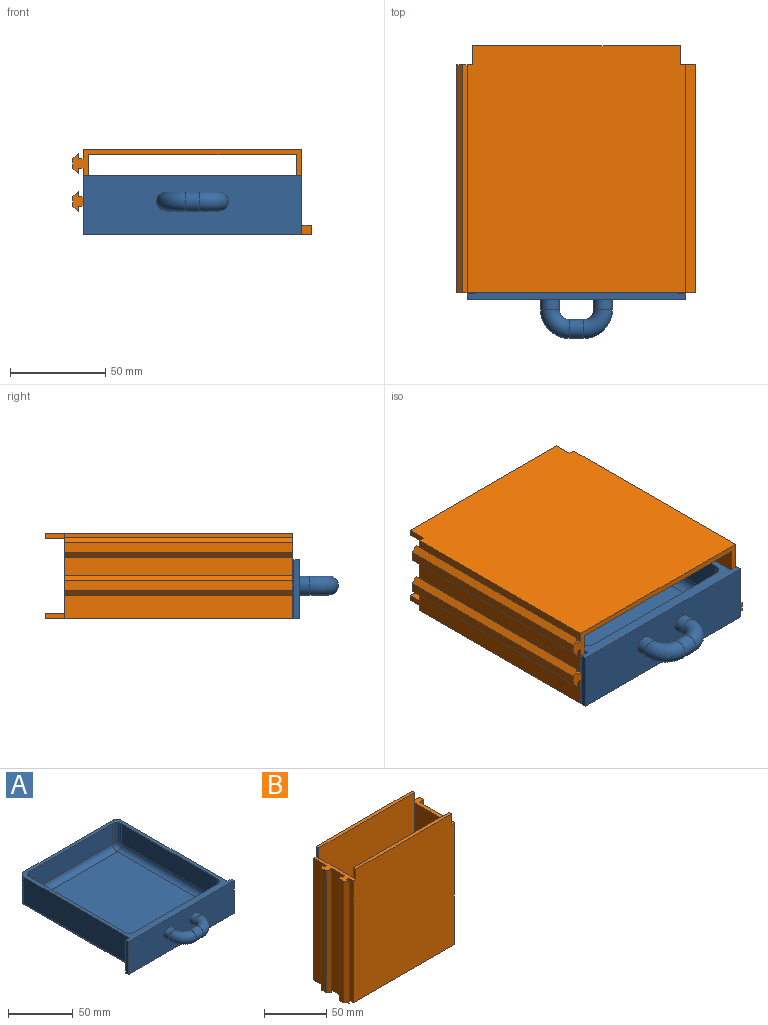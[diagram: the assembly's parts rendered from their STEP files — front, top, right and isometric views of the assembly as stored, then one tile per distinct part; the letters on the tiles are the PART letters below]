
ASSEMBLY  parts=2 mates=2
PART A: 39 faces, bbox 115x145x31 mm
  f0: plane 123x115mm, normal (0,0,1), area 1678.7mm2, adj f2,f3,f4,f6,f7,f8,f9,f10
  f1: plane 118x102.5mm, normal (0,0,-1), area 12091.1mm2, adj f10,f34,f35,f36,f37,f38
  f2: plane 115x25mm, normal (1,0,0), area 2875mm2, adj f0,f10,f27,f38
  f3: plane 115x25mm, normal (-1,0,0), area 2875mm2, adj f0,f10,f28,f34
  f4: plane 96.5x25mm, normal (0,1,0), area 2412.5mm2, adj f0,f27,f28,f36
  f5: plane 104x90.5mm, normal (0,0,1), area 9412mm2, adj f17,f20,f23,f26
  f6: plane 104x19mm, normal (-1,0,0), area 1976mm2, adj f0,f15,f20,f21
  f7: plane 104x19mm, normal (1,0,0), area 1976mm2, adj f0,f16,f22,f23
  f8: plane 90.5x19mm, normal (0,1,0), area 1719.5mm2, adj f0,f21,f22,f26
  f9: plane 90.5x19mm, normal (0,-1,0), area 1719.5mm2, adj f0,f15,f16,f17
  f10: plane 115x31mm, normal (0,1,0), area 691.2mm2, adj f0,f1,f2,f3,f11,f12,f13,f34
  f11: plane 31x3mm, normal (-1,0,0), area 93mm2, adj f0,f10,f12,f14
  f12: plane 115x3mm, normal (0,0,-1), area 345mm2, adj f10,f11,f13,f14
  f13: plane 31x3mm, normal (1,0,0), area 93mm2, adj f0,f10,f12,f14
  f14: plane 115x31mm, normal (0,-1,0), area 3407.9mm2, adj f0,f11,f12,f13,f29,f33
  f15: cylinder r=5mm len=19mm, axis (0,0,-1), area 149.2mm2, adj f0,f6,f9,f18
  f16: cylinder r=5mm len=19mm, axis (0,0,1), area 149.2mm2, adj f0,f7,f9,f19
  f17: cylinder r=5mm len=90.5mm, axis (-1,0,0), area 710.8mm2, adj f5,f9,f18,f19
  f18: sphere r=5mm, area 39.3mm2, adj f15,f17,f20
  f19: sphere r=5mm, area 39.3mm2, adj f16,f17,f23
  f20: cylinder r=5mm len=104mm, axis (0,1,0), area 816.8mm2, adj f5,f6,f18,f24
  f21: cylinder r=5mm len=19mm, axis (0,0,1), area 149.2mm2, adj f0,f6,f8,f24
  f22: cylinder r=5mm len=19mm, axis (0,0,-1), area 149.2mm2, adj f0,f7,f8,f25
  f23: cylinder r=5mm len=104mm, axis (0,-1,0), area 816.8mm2, adj f5,f7,f19,f25
  f24: sphere r=5mm, area 39.3mm2, adj f20,f21,f26
  f25: sphere r=5mm, area 39.3mm2, adj f22,f23,f26
  f26: cylinder r=5mm len=90.5mm, axis (1,0,0), area 710.8mm2, adj f5,f8,f24,f25
  f27: cylinder r=5mm len=25mm, axis (0,0,1), area 196.3mm2, adj f0,f2,f4,f37
  f28: cylinder r=5mm len=25mm, axis (0,0,-1), area 196.3mm2, adj f0,f3,f4,f35
  f29: cylinder r=5mm len=10mm, axis (0,-1,0), area 169.4mm2, adj f14,f30
  f30: torus R=10mm, axis (0,0,1), area 493.5mm2, adj f29,f31
  f31: cylinder r=5mm len=10mm, axis (1,0,0), area 245.2mm2, adj f30,f32
  f32: torus R=10mm, axis (0,0,1), area 493.5mm2, adj f31,f33
  f33: cylinder r=5mm len=10mm, axis (0,1,0), area 169.4mm2, adj f14,f32
  f34: cylinder r=2mm len=115mm, axis (0,1,0), area 361.3mm2, adj f1,f3,f10,f35
  f35: torus R=3mm, axis (0,0,-1), area 21.1mm2, adj f1,f28,f34,f36
  f36: cylinder r=2mm len=96.5mm, axis (1,0,0), area 303.2mm2, adj f1,f4,f35,f37
  f37: torus R=3mm, axis (0,0,-1), area 21.1mm2, adj f1,f27,f36,f38
  f38: cylinder r=2mm len=115mm, axis (0,-1,0), area 361.3mm2, adj f1,f2,f10,f37
PART B: 35 faces, bbox 125.5x45x130 mm
  f0: plane 130x120mm, normal (0,1,0), area 15490mm2, adj f14,f20,f24,f28,f29,f31,f32,f34
  f1: plane 120x3mm, normal (-0.71,-0.71,0), area 509.1mm2, adj f2,f18,f28,f31
  f2: plane 120x5mm, normal (-1,0,0), area 600mm2, adj f1,f3,f28,f31
  f3: plane 120x3mm, normal (-0.71,0.71,0), area 509.1mm2, adj f2,f4,f28,f31
  f4: plane 120x3mm, normal (1,0,0), area 360mm2, adj f3,f5,f28,f31
  f5: plane 120x2.5mm, normal (0,1,0), area 300mm2, adj f4,f6,f28,f31
  f6: plane 120x15mm, normal (-1,0,0), area 1800mm2, adj f5,f7,f28,f31
  f7: plane 120x2.5mm, normal (0,-1,0), area 300mm2, adj f6,f8,f28,f31
  f8: plane 120x3mm, normal (1,0,0), area 360mm2, adj f7,f9,f28,f31
  f9: plane 120x3mm, normal (-0.71,-0.71,0), area 509.1mm2, adj f8,f10,f28,f31
  f10: plane 120x5mm, normal (-1,0,0), area 600mm2, adj f9,f11,f28,f31
  f11: plane 120x3mm, normal (-0.71,0.71,0), area 509.1mm2, adj f10,f12,f28,f31
  f12: plane 120x3mm, normal (1,0,0), area 360mm2, adj f11,f13,f28,f31
  f13: plane 120x2.5mm, normal (0,1,0), area 300mm2, adj f12,f14,f28,f31
  f14: plane 120x15mm, normal (-1,0,0), area 1800mm2, adj f0,f13,f28,f31
  f15: plane 130x115mm, normal (0,-1,0), area 14890mm2, adj f16,f19,f26,f28,f30,f31,f33,f34
  f16: plane 120x5mm, normal (-1,0,0), area 600mm2, adj f15,f17,f28,f31
  f17: plane 120x2.5mm, normal (0,-1,0), area 300mm2, adj f16,f18,f28,f31
  f18: plane 120x3mm, normal (1,0,0), area 360mm2, adj f1,f17,f28,f31
  f19: plane 109x3mm, normal (0,0,1), area 327mm2, adj f15,f27,f30,f33
  f20: plane 109x3mm, normal (0,0,1), area 327mm2, adj f0,f22,f29,f32
  f21: plane 120x39mm, normal (-1,0,0), area 4680mm2, adj f22,f27,f28,f34
  f22: plane 130x109mm, normal (0,-1,0), area 14170mm2, adj f20,f21,f23,f28,f29,f32
  f23: plane 120x39mm, normal (1,0,0), area 4680mm2, adj f22,f27,f28,f31
  f24: plane 120x5mm, normal (1,0,0), area 600mm2, adj f0,f25,f28,f34
  f25: plane 120x5mm, normal (0,-1,0), area 600mm2, adj f24,f26,f28,f34
  f26: plane 120x40mm, normal (1,0,0), area 4800mm2, adj f15,f25,f28,f34
  f27: plane 130x109mm, normal (0,1,0), area 14170mm2, adj f19,f21,f23,f28,f30,f33
  f28: plane 125.5x45mm, normal (0,0,-1), area 1022mm2, adj f0,f1,f2,f3,f4,f5,f6,f7
  f29: plane 10x3mm, normal (-1,0,0), area 30mm2, adj f0,f20,f22,f31
  f30: plane 10x3mm, normal (-1,0,0), area 30mm2, adj f15,f19,f27,f31
  f31: plane 45x8.5mm, normal (0,0,1), area 208mm2, adj f0,f1,f2,f3,f4,f5,f6,f7
  f32: plane 10x3mm, normal (1,0,0), area 30mm2, adj f0,f20,f22,f34
  f33: plane 10x3mm, normal (1,0,0), area 30mm2, adj f15,f19,f27,f34
  f34: plane 45x8mm, normal (0,0,1), area 160mm2, adj f0,f15,f21,f24,f25,f26,f32,f33
PLACE A t=(-115.79,28.99,-59.32)mm
PLACE B rot(axis=(-1,0,0),90deg) t=(-115.79,-90.36,-36.82)mm
MATE slider B.f28 <-> A.f10  axis (0,-1,0) through (-173.29,-90.36,-76.82)mm
MATE fastened B.f22 <-> B.f22  axis (0,0,1) through (-115.79,-90.36,-73.82)mm
